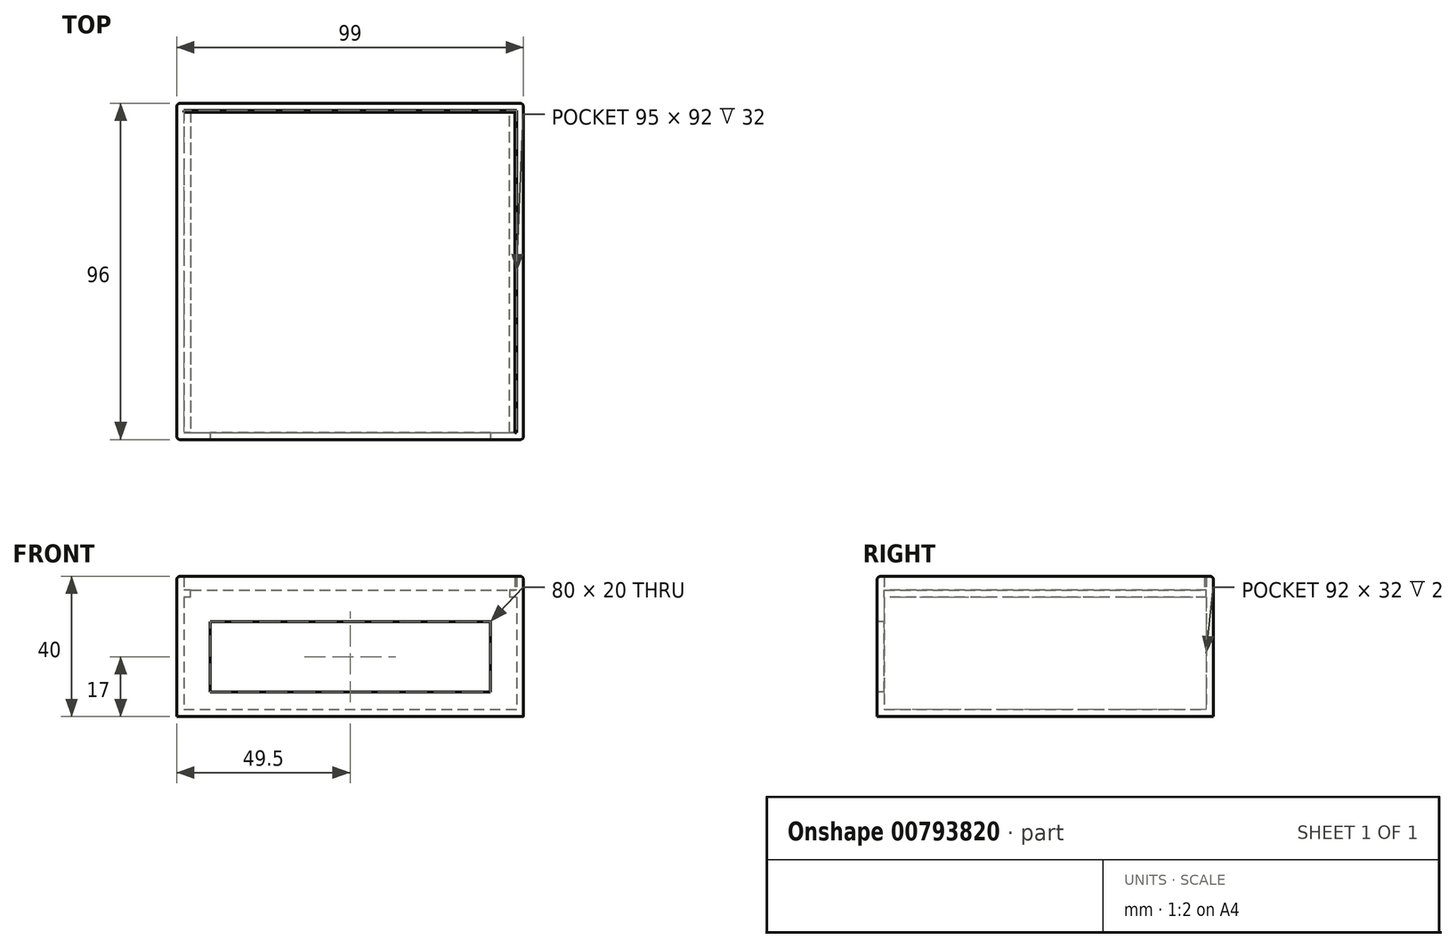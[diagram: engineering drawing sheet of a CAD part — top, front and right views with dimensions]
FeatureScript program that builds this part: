
annotation { "Feature Type Name" : "Feature", "Feature Type Description" : "" }
export const myFeature = defineFeature(function(context is Context, id is Id, definition is map)
    precondition{}
    {
        {
            var Q0;
            Q0=qCreatedBy(makeId("Top.planeOp"),FACE);
            var sketch = newSketch(context, id + "F0", { "sketchPlane" : qUnion([Q0])});
            skLineSegment(sketch, "E0.bottom", {"start": v(-49.5, -48) * mm, "end": v(49.5, -48) * mm});
            skLineSegment(sketch, "E0.top", {"start": v(-49.5, 48) * mm, "end": v(49.5, 48) * mm});
            skLineSegment(sketch, "E0.left", {"start": v(-49.5, -48) * mm, "end": v(-49.5, 48) * mm});
            skLineSegment(sketch, "E0.right", {"start": v(49.5, -48) * mm, "end": v(49.5, 48) * mm});
            skPoint(sketch, "E0.middle", {"position": v(0, 0) * mm});
            skLineSegment(sketch, "E1.0", {"start": v(-47.5, -46) * mm, "end": v(-47.5, 46) * mm});
            skLineSegment(sketch, "E2.0", {"start": v(-47.5, 46) * mm, "end": v(47.5, 46) * mm});
            skLineSegment(sketch, "E3.0", {"start": v(47.5, -46) * mm, "end": v(47.5, 46) * mm});
            skLineSegment(sketch, "E4.0", {"start": v(-47.5, -46) * mm, "end": v(47.5, -46) * mm});
            skSolve(sketch);
        }
        {
            var Q0;
            Q0=makeQuery(id+"F0.imprint","IMPRINT",FACE,{"disambiguationData":[TD([[makeQuery(id+"F0.imprint","IMPRINT",EDGE,{"derivedFrom":sQuery(id+"F0.wireOp",EDGE,"E0.bottom")}),1.0]])]});
            extrude(context, id + "F1", {"entities" : qUnion([Q0]), "depth" : 40 * mm, "offsetDistance" : 25 * mm});
        }
        {
            var Q0;
            Q0=makeQuery(id+"F0.imprint","IMPRINT",FACE,{"disambiguationData":[TD([[makeQuery(id+"F0.imprint","IMPRINT",EDGE,{"derivedFrom":sQuery(id+"F0.wireOp",EDGE,"E1.0")}),-1.0]])]});
            extrude(context, id + "F2", {"entities" : qUnion([Q0]), "operationType" : NewBodyOperationType.ADD, "depth" : 2 * mm, "offsetDistance" : 25 * mm});
        }
        {
            var Q0;
            Q0=makeQuery(id+"F1.opExtrude","SWEPT_FACE",FACE,{"disambiguationData":[OSD([sQuery(id+"F0.wireOp",EDGE,"E0.bottom")])]});
            var sketch = newSketch(context, id + "F3", { "sketchPlane" : qUnion([Q0])});
            skLineSegment(sketch, "E5.bottom", {"start": v(40, 7) * mm, "end": v(-40, 7) * mm});
            skLineSegment(sketch, "E5.top", {"start": v(40, 27) * mm, "end": v(-40, 27) * mm});
            skLineSegment(sketch, "E5.left", {"start": v(40, 7) * mm, "end": v(40, 27) * mm});
            skLineSegment(sketch, "E5.right", {"start": v(-40, 7) * mm, "end": v(-40, 27) * mm});
            skPoint(sketch, "E5.middle", {"position": v(0, 17) * mm});
            skSolve(sketch);
        }
        {
            var Q0;
            Q0=makeQuery(id+"F3.imprint","IMPRINT",FACE,{"disambiguationData":[TD([[makeQuery(id+"F3.imprint","IMPRINT",EDGE,{"derivedFrom":sQuery(id+"F3.wireOp",EDGE,"E5.bottom")}),-1.0]])]});
            extrude(context, id + "F4", {"entities" : qUnion([Q0]), "operationType" : NewBodyOperationType.REMOVE, "oppositeDirection" : true, "depth" : 2 * mm, "offsetDistance" : 25 * mm});
        }
        {
            var Q0;
            Q0=makeQuery(id+"F1.opExtrude","CAP_EDGE",EDGE,{"disambiguationData":[OSD([sQuery(id+"F0.wireOp",EDGE,"E0.left")])],"isStart":false});
            var Q1;
            Q1=makeQuery(id+"F1.opExtrude","CAP_EDGE",EDGE,{"disambiguationData":[OSD([sQuery(id+"F0.wireOp",EDGE,"E0.bottom")])],"isStart":false});
            var Q2;
            Q2=makeQuery(id+"F1.opExtrude","CAP_EDGE",EDGE,{"disambiguationData":[OSD([sQuery(id+"F0.wireOp",EDGE,"E0.right")])],"isStart":false});
            var Q3;
            Q3=makeQuery(id+"F1.opExtrude","CAP_EDGE",EDGE,{"disambiguationData":[OSD([sQuery(id+"F0.wireOp",EDGE,"E0.top")])],"isStart":false});
            var Q4;
            Q4=makeQuery(id+"F1.opExtrude","SWEPT_EDGE",EDGE,{"disambiguationData":[OSD([sQuery(id+"F0.wireOp",EDGE,"E0.bottom"),sQuery(id+"F0.wireOp",EDGE,"E0.left")])]});
            var Q5;
            Q5=makeQuery(id+"F1.opExtrude","SWEPT_EDGE",EDGE,{"disambiguationData":[OSD([sQuery(id+"F0.wireOp",EDGE,"E0.bottom"),sQuery(id+"F0.wireOp",EDGE,"E0.right")])]});
            var Q6;
            Q6=makeQuery(id+"F1.opExtrude","SWEPT_EDGE",EDGE,{"disambiguationData":[OSD([sQuery(id+"F0.wireOp",EDGE,"E0.top"),sQuery(id+"F0.wireOp",EDGE,"E0.right")])]});
            var Q7;
            Q7=makeQuery(id+"F1.opExtrude","SWEPT_EDGE",EDGE,{"disambiguationData":[OSD([sQuery(id+"F0.wireOp",EDGE,"E0.top"),sQuery(id+"F0.wireOp",EDGE,"E0.left")])]});
            fillet(context, id + "F5", {"entities" : qUnion([Q0, Q1, Q2, Q3, Q4, Q5, Q6, Q7]), "radius" : 1 * mm, "tangentPropagation" : true, "allowEdgeOverflow" : false});
        }
        {
            var Q0;
            Q0=makeQuery(id+"F1.opExtrude","SWEPT_FACE",FACE,{"disambiguationData":[OSD([sQuery(id+"F0.wireOp",EDGE,"E0.right")])]});
            var sketch = newSketch(context, id + "F6", { "sketchPlane" : qUnion([Q0])});
            skLineSegment(sketch, "E6.bottom", {"start": v(-47, 34) * mm, "end": v(47, 34) * mm});
            skLineSegment(sketch, "E6.top", {"start": v(-47, 36) * mm, "end": v(47, 36) * mm});
            skLineSegment(sketch, "E6.left", {"start": v(-47, 34) * mm, "end": v(-47, 36) * mm});
            skLineSegment(sketch, "E6.right", {"start": v(47, 34) * mm, "end": v(47, 36) * mm});
            skSolve(sketch);
        }
        {
            var Q0;
            Q0 = qSketchRegion(id + "F6", true);
            extrude(context, id + "F7", {"entities" : qUnion([Q0]), "operationType" : NewBodyOperationType.ADD, "oppositeDirection" : true, "depth" : 4 * mm, "offsetDistance" : 25 * mm});
        }
        {
            var Q0;
            Q0=makeQuery(id+"F1.opExtrude","SWEPT_FACE",FACE,{"disambiguationData":[OSD([sQuery(id+"F0.wireOp",EDGE,"E0.left")])]});
            var sketch = newSketch(context, id + "F8", { "sketchPlane" : qUnion([Q0])});
            skLineSegment(sketch, "E7.bottom", {"start": v(-47, 36) * mm, "end": v(47, 36) * mm});
            skLineSegment(sketch, "E7.top", {"start": v(-47, 34) * mm, "end": v(47, 34) * mm});
            skLineSegment(sketch, "E7.left", {"start": v(-47, 36) * mm, "end": v(-47, 34) * mm});
            skLineSegment(sketch, "E7.right", {"start": v(47, 36) * mm, "end": v(47, 34) * mm});
            skSolve(sketch);
        }
        {
            var Q0;
            Q0=makeQuery(id+"F8.imprint","IMPRINT",FACE,{"disambiguationData":[TD([[makeQuery(id+"F8.imprint","IMPRINT",EDGE,{"derivedFrom":sQuery(id+"F8.wireOp",EDGE,"E7.bottom")}),-1.0]])]});
            extrude(context, id + "F9", {"entities" : qUnion([Q0]), "operationType" : NewBodyOperationType.ADD, "oppositeDirection" : true, "depth" : 4 * mm, "offsetDistance" : 25 * mm});
        }
        {
            var Q0;
            Q0=makeQuery(id+"F9.opExtrude","SWEPT_FACE",FACE,{"disambiguationData":[OSD([sQuery(id+"F8.wireOp",EDGE,"E7.bottom")])]});
            var sketch = newSketch(context, id + "F10", { "sketchPlane" : qUnion([Q0])});
            skLineSegment(sketch, "E8.bottom", {"start": v(-47.5, -46) * mm, "end": v(47, -46) * mm});
            skLineSegment(sketch, "E8.top", {"start": v(-47.5, 45.5) * mm, "end": v(47, 45.5) * mm});
            skLineSegment(sketch, "E8.left", {"start": v(-47.5, -46) * mm, "end": v(-47.5, 45.5) * mm});
            skLineSegment(sketch, "E8.right", {"start": v(47, -46) * mm, "end": v(47, 45.5) * mm});
            skSolve(sketch);
        }
        {
            var Q0;
            Q0 = qSketchRegion(id + "F10", true);
            extrude(context, id + "F11", {"entities" : qUnion([Q0]), "operationType" : NewBodyOperationType.ADD, "depth" : 4 * mm, "offsetDistance" : 25 * mm});
        }
    });
